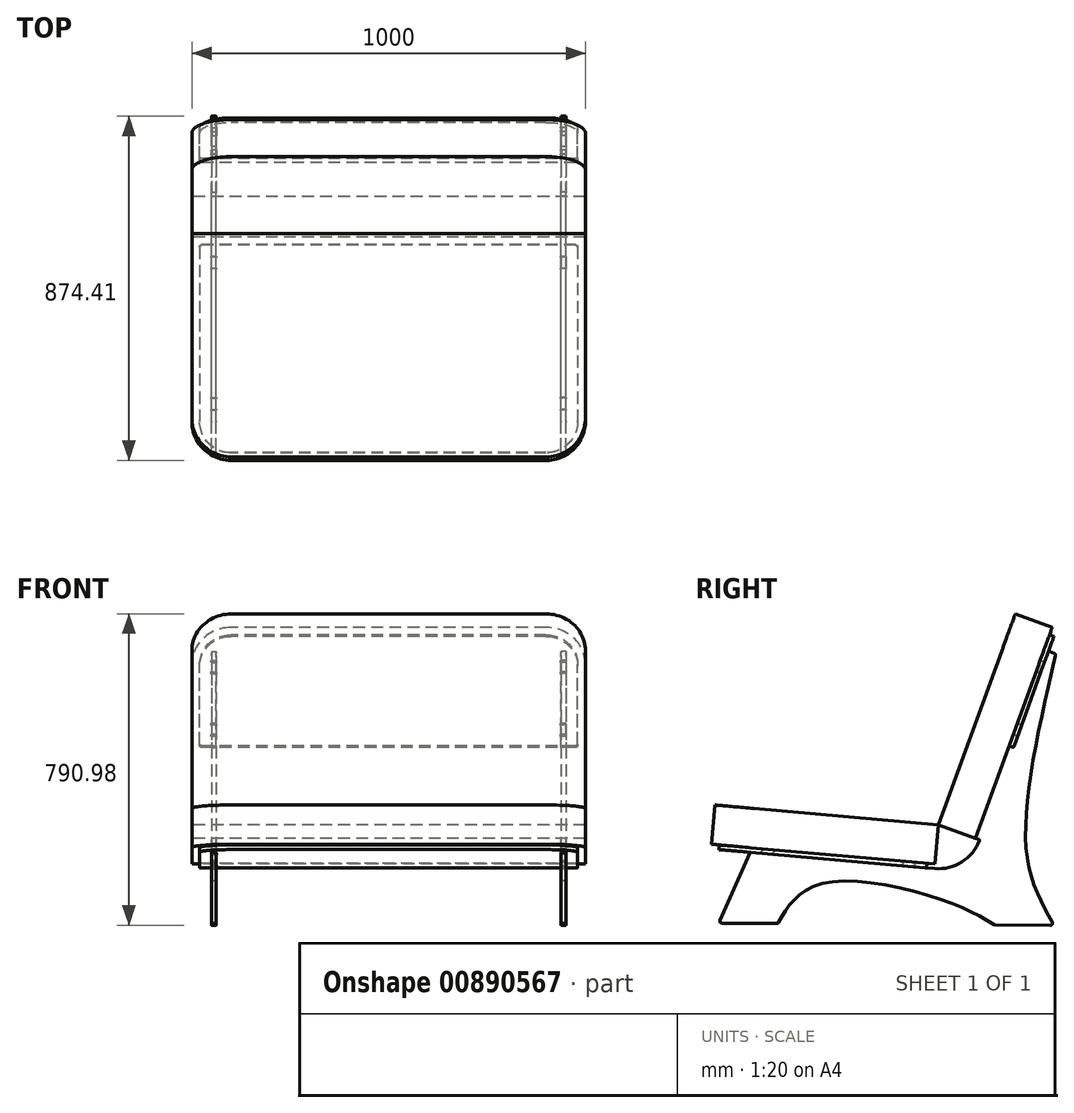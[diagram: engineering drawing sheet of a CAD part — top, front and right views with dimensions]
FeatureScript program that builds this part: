
annotation { "Feature Type Name" : "Feature", "Feature Type Description" : "" }
export const myFeature = defineFeature(function(context is Context, id is Id, definition is map)
    precondition{}
    {
        {
            var Q0;
            Q0=qCreatedBy(makeId("Right.planeOp"),FACE);
            var sketch = newSketch(context, id + "F0", { "sketchPlane" : qUnion([Q0])});
            skLineSegment(sketch, "E0", {"start": v(-759.48, 0) * mm, "end": v(436.3, 0) * mm, "construction": true});
            skLineSegment(sketch, "E1", {"start": v(0, 0) * mm, "end": v(-567.8, 50) * mm});
            skLineSegment(sketch, "E2", {"start": v(-567.8, 50) * mm, "end": v(-567.8, 0) * mm, "construction": true});
            skLineSegment(sketch, "E3.0", {"start": v(8.77, 99.61) * mm, "end": v(-559.03, 149.61) * mm});
            skLineSegment(sketch, "E4", {"start": v(-559.03, 149.61) * mm, "end": v(-567.8, 50) * mm});
            skLineSegment(sketch, "E5", {"start": v(8.77, 99.61) * mm, "end": v(0, 0) * mm});
            skLineSegment(sketch, "E6", {"start": v(8.77, 99.61) * mm, "end": v(204.03, 635.13) * mm});
            skLineSegment(sketch, "E7.0", {"start": v(102.72, 65.36) * mm, "end": v(297.98, 600.87) * mm});
            skLineSegment(sketch, "E8", {"start": v(204.03, 635.13) * mm, "end": v(297.98, 600.87) * mm});
            skLineSegment(sketch, "E9", {"start": v(8.77, 99.61) * mm, "end": v(102.72, 65.36) * mm});
            skSolve(sketch);
        }
        {
            var Q0;
            Q0=makeQuery(id+"F0.imprint","IMPRINT",FACE,{"disambiguationData":[TD([[makeQuery(id+"F0.imprint","IMPRINT",EDGE,{"derivedFrom":sQuery(id+"F0.wireOp",EDGE,"E1")}),-1.0]])]});
            var Q1;
            Q1=makeQuery(id+"F0.imprint","IMPRINT",FACE,{"disambiguationData":[TD([[makeQuery(id+"F0.imprint","IMPRINT",EDGE,{"derivedFrom":sQuery(id+"F0.wireOp",EDGE,"E6")}),-1.0]])]});
            extrude(context, id + "F1", {"entities" : qUnion([Q0, Q1]), "depth" : 500 * mm, "offsetDistance" : 25 * mm, "hasSecondDirection" : true, "secondDirectionOppositeDirection" : true, "secondDirectionDepth" : 500 * mm});
        }
        {
            var Q0;
            Q0=makeQuery(id+"F1.opExtrude","CAP_EDGE",EDGE,{"disambiguationData":[OSD([sQuery(id+"F0.wireOp",EDGE,"E4")])],"isStart":true});
            var Q1;
            Q1=makeQuery(id+"F1.opExtrude","CAP_EDGE",EDGE,{"disambiguationData":[OSD([sQuery(id+"F0.wireOp",EDGE,"E4")])],"isStart":false});
            var Q2;
            Q2=makeQuery(id+"F1.opExtrude","CAP_EDGE",EDGE,{"disambiguationData":[OSD([sQuery(id+"F0.wireOp",EDGE,"E8")])],"isStart":false});
            var Q3;
            Q3=makeQuery(id+"F1.opExtrude","CAP_EDGE",EDGE,{"disambiguationData":[OSD([sQuery(id+"F0.wireOp",EDGE,"E8")])],"isStart":true});
            fillet(context, id + "F2", {"entities" : qUnion([Q0, Q1, Q2, Q3]), "radius" : 100 * mm, "tangentPropagation" : true, "allowEdgeOverflow" : false});
        }
        {
            var Q0;
            Q0=makeQuery(id+"F1.opExtrude","SWEPT_FACE",FACE,{"disambiguationData":[OSD([sQuery(id+"F0.wireOp",EDGE,"E1")])]});
            var sketch = newSketch(context, id + "F3", { "sketchPlane" : qUnion([Q0])});
            skLineSegment(sketch, "E10.0", {"start": v(480, 20) * mm, "end": v(480, 470) * mm});
            skLineSegment(sketch, "E10.1", {"start": v(-480, 20) * mm, "end": v(-480, 470) * mm});
            skArc(sketch, "E10.2", {"start": v(-400, 550) * mm, "mid": v(-456.57, 526.57) * mm, "end": v(-480, 470) * mm});
            skLineSegment(sketch, "E10.3", {"start": v(480, 20) * mm, "end": v(-480, 20) * mm});
            skLineSegment(sketch, "E10.4", {"start": v(400, 550) * mm, "end": v(-400, 550) * mm});
            skArc(sketch, "E10.5", {"start": v(480, 470) * mm, "mid": v(456.57, 526.57) * mm, "end": v(400, 550) * mm});
            skSolve(sketch);
        }
        {
            var Q0;
            Q0=makeQuery(id+"F3.imprint","IMPRINT",FACE,{"disambiguationData":[TD([[makeQuery(id+"F3.imprint","IMPRINT",EDGE,{"derivedFrom":sQuery(id+"F3.wireOp",EDGE,"E10.0")}),1.0]])]});
            extrude(context, id + "F4", {"entities" : qUnion([Q0]), "depth" : 12 * mm, "offsetDistance" : 25 * mm});
        }
        {
            var Q0;
            Q0=makeQuery(id+"F1.opExtrude","SWEPT_FACE",FACE,{"disambiguationData":[OSD([sQuery(id+"F0.wireOp",EDGE,"E7.0")])]});
            var sketch = newSketch(context, id + "F5", { "sketchPlane" : qUnion([Q0])});
            skArc(sketch, "E11.1", {"start": v(-400, 646.6) * mm, "mid": v(-456.57, 623.16) * mm, "end": v(-480, 566.6) * mm});
            skLineSegment(sketch, "E11.2", {"start": v(-400, 646.6) * mm, "end": v(400, 646.6) * mm});
            skLineSegment(sketch, "E11.3", {"start": v(-480, 346.6) * mm, "end": v(-480, 566.6) * mm});
            skArc(sketch, "E11.4", {"start": v(480, 566.6) * mm, "mid": v(456.57, 623.16) * mm, "end": v(400, 646.6) * mm});
            skLineSegment(sketch, "E11.5", {"start": v(480, 346.6) * mm, "end": v(480, 566.6) * mm});
            skLineSegment(sketch, "E12.0", {"start": v(-480, 346.6) * mm, "end": v(480, 346.6) * mm});
            skSolve(sketch);
        }
        {
            var Q0;
            Q0=makeQuery(id+"F5.imprint","IMPRINT",FACE,{"disambiguationData":[TD([[makeQuery(id+"F5.imprint","IMPRINT",EDGE,{"derivedFrom":sQuery(id+"F5.wireOp",EDGE,"E11.1")}),1.0]])]});
            extrude(context, id + "F6", {"entities" : qUnion([Q0]), "depth" : 12 * mm, "offsetDistance" : 25 * mm});
        }
        {
            var Q0;
            Q0=qCreatedBy(makeId("Right.planeOp"),FACE);
            var sketch = newSketch(context, id + "F7", { "sketchPlane" : qUnion([Q0])});
            skLineSegment(sketch, "E13.0.0", {"start": v(-19.92, 1.75) * mm, "end": v(-468.19, 41.23) * mm, "construction": true});
            skLineSegment(sketch, "E13.0.1", {"start": v(-468.19, 41.23) * mm, "end": v(-469.24, 29.27) * mm, "construction": true});
            skLineSegment(sketch, "E13.0.2", {"start": v(-469.24, 29.27) * mm, "end": v(-20.98, -10.2) * mm, "construction": true});
            skLineSegment(sketch, "E13.0.3", {"start": v(-20.98, -10.2) * mm, "end": v(-19.92, 1.75) * mm, "construction": true});
            skLineSegment(sketch, "E14.0.0", {"start": v(204.03, 635.13) * mm, "end": v(169.77, 541.18) * mm, "construction": true});
            skLineSegment(sketch, "E14.0.3", {"start": v(297.98, 600.87) * mm, "end": v(204.03, 635.13) * mm, "construction": true});
            skLineSegment(sketch, "E14.1.2", {"start": v(169.77, 541.18) * mm, "end": v(8.77, 99.61) * mm, "construction": true});
            skLineSegment(sketch, "E14.1.3", {"start": v(8.77, 99.61) * mm, "end": v(102.72, 65.36) * mm, "construction": true});
            skLineSegment(sketch, "E14.2.0", {"start": v(8.77, 99.61) * mm, "end": v(-459.42, 140.84) * mm, "construction": true});
            skLineSegment(sketch, "E14.2.1", {"start": v(-459.42, 140.84) * mm, "end": v(-468.19, 41.23) * mm, "construction": true});
            skLineSegment(sketch, "E14.2.2", {"start": v(-468.19, 41.23) * mm, "end": v(0, 0) * mm, "construction": true});
            skLineSegment(sketch, "E14.2.3", {"start": v(0, 0) * mm, "end": v(8.77, 99.61) * mm, "construction": true});
            skLineSegment(sketch, "E14.3.0", {"start": v(-559.03, 149.61) * mm, "end": v(-459.42, 140.84) * mm, "construction": true});
            skLineSegment(sketch, "E14.3.1", {"start": v(-567.8, 50) * mm, "end": v(-559.03, 149.61) * mm, "construction": true});
            skLineSegment(sketch, "E14.3.2", {"start": v(-567.8, 50) * mm, "end": v(-468.19, 41.23) * mm, "construction": true});
            skLineSegment(sketch, "E14.3.3", {"start": v(-468.19, 41.23) * mm, "end": v(-459.42, 140.84) * mm, "construction": true});
            skLineSegment(sketch, "E15.0", {"start": v(-759.48, 0) * mm, "end": v(436.3, 0) * mm, "construction": true});
            skLineSegment(sketch, "E16", {"start": v(-559.03, 149.61) * mm, "end": v(812.25, 140.84) * mm, "construction": true});
            skLineSegment(sketch, "E17.0", {"start": v(-560.95, -150.38) * mm, "end": v(810.34, -159.15) * mm, "construction": true});
            skLineSegment(sketch, "E18.0.0", {"start": v(-468.19, 41.23) * mm, "end": v(-547.88, 48.25) * mm, "construction": true});
            skLineSegment(sketch, "E18.0.1", {"start": v(-547.88, 48.25) * mm, "end": v(-548.93, 36.3) * mm, "construction": true});
            skLineSegment(sketch, "E18.0.2", {"start": v(-548.93, 36.3) * mm, "end": v(-469.24, 29.27) * mm, "construction": true});
            skLineSegment(sketch, "E19.0.0", {"start": v(291.13, 582.08) * mm, "end": v(263.72, 506.92) * mm, "construction": true});
            skLineSegment(sketch, "E19.0.3", {"start": v(302.4, 577.97) * mm, "end": v(291.13, 582.08) * mm, "construction": true});
            skLineSegment(sketch, "E20", {"start": v(-548.93, 36.3) * mm, "end": v(-548.93, -280.6) * mm, "construction": true});
            skLineSegment(sketch, "E21", {"start": v(-548.93, -150.46) * mm, "end": v(-469.24, 29.27) * mm});
            skLineSegment(sketch, "E22", {"start": v(302.4, 577.97) * mm, "end": v(302.4, -479.36) * mm, "construction": true});
            skLineSegment(sketch, "E23", {"start": v(-469.24, 29.27) * mm, "end": v(-439.36, 26.64) * mm});
            skLineSegment(sketch, "E24", {"start": v(-439.36, 26.64) * mm, "end": v(-438.3, 38.6) * mm});
            skLineSegment(sketch, "E25", {"start": v(-438.3, 38.6) * mm, "end": v(-408.42, 35.96) * mm});
            skLineSegment(sketch, "E26", {"start": v(-408.42, 35.96) * mm, "end": v(-409.47, 24.01) * mm});
            skLineSegment(sketch, "E27", {"start": v(-20.98, -10.2) * mm, "end": v(-50.86, -7.57) * mm});
            skLineSegment(sketch, "E28", {"start": v(-50.86, -7.57) * mm, "end": v(-49.8, 4.39) * mm});
            skLineSegment(sketch, "E29", {"start": v(-49.8, 4.39) * mm, "end": v(-79.7, 7.02) * mm});
            skLineSegment(sketch, "E30", {"start": v(-79.7, 7.02) * mm, "end": v(-80.74, -4.94) * mm});
            skLineSegment(sketch, "E31", {"start": v(-80.74, -4.94) * mm, "end": v(-409.47, 24.01) * mm});
            skLineSegment(sketch, "E32", {"start": v(-548.93, -150.46) * mm, "end": v(-398.94, -151.42) * mm});
            skLineSegment(sketch, "E33", {"start": v(302.4, -155.9) * mm, "end": v(152.4, -154.94) * mm});
            skFitSpline(sketch, "E34", {"points": [v(-398.94, -151.42) * mm, v(-357.7, -91.47) * mm, v(-259.83, -45.2) * mm, v(19.54, -91.47) * mm, v(152.4, -154.94) * mm], "startDerivative": vector(200.43, 350.59) * mm, "endDerivative": vector(440.32, -254.58) * mm});
            skLineSegment(sketch, "E35", {"start": v(302.4, 577.97) * mm, "end": v(288.7, 540.4) * mm, "construction": true});
            skLineSegment(sketch, "E36", {"start": v(199.63, 296.12) * mm, "end": v(209.91, 324.3) * mm});
            skLineSegment(sketch, "E37", {"start": v(209.91, 324.3) * mm, "end": v(198.64, 328.42) * mm});
            skLineSegment(sketch, "E38", {"start": v(198.64, 328.42) * mm, "end": v(208.91, 356.6) * mm});
            skLineSegment(sketch, "E39", {"start": v(208.91, 356.6) * mm, "end": v(220.19, 352.5) * mm});
            skLineSegment(sketch, "E40", {"start": v(288.7, 540.4) * mm, "end": v(307.49, 533.54) * mm});
            skFitSpline(sketch, "E41", {"points": [v(307.49, 533.54) * mm, v(232.67, 31.44) * mm, v(302.4, -155.9) * mm], "startDerivative": vector(-214.75, -918.96) * mm, "endDerivative": vector(239.2, -422.01) * mm});
            skLineSegment(sketch, "E42", {"start": v(288.7, 540.4) * mm, "end": v(278.42, 512.2) * mm});
            skLineSegment(sketch, "E43", {"start": v(278.42, 512.2) * mm, "end": v(267.15, 516.32) * mm});
            skLineSegment(sketch, "E44", {"start": v(267.15, 516.32) * mm, "end": v(256.87, 488.13) * mm});
            skLineSegment(sketch, "E45", {"start": v(256.87, 488.13) * mm, "end": v(268.14, 484.02) * mm});
            skLineSegment(sketch, "E46", {"start": v(268.14, 484.02) * mm, "end": v(220.19, 352.5) * mm});
            skLineSegment(sketch, "E47", {"start": v(-20.98, -10.2) * mm, "end": v(-1.05, -11.95) * mm});
            skLineSegment(sketch, "E48", {"start": v(102.72, 65.36) * mm, "end": v(256.87, 488.13) * mm, "construction": true});
            skLineSegment(sketch, "E49", {"start": v(199.63, 296.12) * mm, "end": v(188.36, 300.23) * mm});
            skLineSegment(sketch, "E50", {"start": v(188.36, 300.23) * mm, "end": v(102.72, 65.36) * mm});
            skLineSegment(sketch, "E51", {"start": v(102.72, 65.36) * mm, "end": v(114, 61.25) * mm});
            skArc(sketch, "E52.trimOffspring", {"start": v(-1.05, -11.95) * mm, "mid": v(68.9, 5.12) * mm, "end": v(114, 61.25) * mm});
            skSolve(sketch);
        }
        {
            var Q0;
            Q0=makeQuery(id+"F7.imprint","IMPRINT",FACE,{"disambiguationData":[TD([[makeQuery(id+"F7.imprint","IMPRINT",EDGE,{"derivedFrom":sQuery(id+"F7.wireOp",EDGE,"E21")}),-1.0]])]});
            extrude(context, id + "F8", {"entities" : qUnion([Q0]), "depth" : 450 * mm, "offsetDistance" : 25 * mm, "hasSecondDirection" : true, "secondDirectionOppositeDirection" : false, "secondDirectionDepth" : 438 * mm});
        }
        {
            var Q0;
            Q0=makeQuery(id+"F8.opExtrude","SWEPT_FACE",FACE,{"disambiguationData":[OSD([sQuery(id+"F7.wireOp",EDGE,"E29")])]});
            var sketch = newSketch(context, id + "F9", { "sketchPlane" : qUnion([Q0])});
            skArc(sketch, "E53", {"start": v(438, -79) * mm, "mid": v(437.3, -80.7) * mm, "end": v(439, -80) * mm});
            skArc(sketch, "E54", {"start": v(439, -50) * mm, "mid": v(437.3, -49.3) * mm, "end": v(438, -51) * mm});
            skArc(sketch, "E55", {"start": v(450, -51) * mm, "mid": v(450.7, -49.3) * mm, "end": v(449, -50) * mm});
            skArc(sketch, "E56", {"start": v(449, -80) * mm, "mid": v(450.7, -80.7) * mm, "end": v(450, -79) * mm});
            skLineSegment(sketch, "E57.bottom", {"start": v(439, -80) * mm, "end": v(449, -80) * mm});
            skLineSegment(sketch, "E57.top", {"start": v(439, -50) * mm, "end": v(449, -50) * mm});
            skLineSegment(sketch, "E57.left", {"start": v(438, -79) * mm, "end": v(438, -51) * mm});
            skLineSegment(sketch, "E57.right", {"start": v(450, -79) * mm, "end": v(450, -51) * mm});
            skLineSegment(sketch, "E58.0", {"start": v(438, -439) * mm, "end": v(438, -411) * mm});
            skLineSegment(sketch, "E58.1", {"start": v(449, -440) * mm, "end": v(439, -440) * mm});
            skLineSegment(sketch, "E58.2", {"start": v(449, -410) * mm, "end": v(439, -410) * mm});
            skLineSegment(sketch, "E58.3", {"start": v(450, -439) * mm, "end": v(450, -411) * mm});
            skArc(sketch, "E59", {"start": v(438, -439) * mm, "mid": v(437.3, -440.7) * mm, "end": v(439, -440) * mm});
            skArc(sketch, "E60", {"start": v(439, -410) * mm, "mid": v(437.3, -409.3) * mm, "end": v(438, -411) * mm});
            skArc(sketch, "E61", {"start": v(450, -411) * mm, "mid": v(450.7, -409.3) * mm, "end": v(449, -410) * mm});
            skArc(sketch, "E62", {"start": v(449, -440) * mm, "mid": v(450.7, -440.7) * mm, "end": v(450, -439) * mm});
            skArc(sketch, "E63.MirrorCS", {"start": v(-450, -411) * mm, "mid": v(-450.7, -409.3) * mm, "end": v(-449, -410) * mm});
            skLineSegment(sketch, "E64.MirrorCS", {"start": v(-449, -410) * mm, "end": v(-439, -410) * mm});
            skArc(sketch, "E65.MirrorCS", {"start": v(-439, -410) * mm, "mid": v(-437.3, -409.3) * mm, "end": v(-438, -411) * mm});
            skLineSegment(sketch, "E66.MirrorCS", {"start": v(-450, -439) * mm, "end": v(-450, -411) * mm});
            skArc(sketch, "E67.MirrorCS", {"start": v(-449, -440) * mm, "mid": v(-450.7, -440.7) * mm, "end": v(-450, -439) * mm});
            skLineSegment(sketch, "E68.MirrorCS", {"start": v(-438, -439) * mm, "end": v(-438, -411) * mm});
            skArc(sketch, "E69.MirrorCS", {"start": v(-438, -439) * mm, "mid": v(-437.3, -440.7) * mm, "end": v(-439, -440) * mm});
            skLineSegment(sketch, "E70.MirrorCS", {"start": v(-449, -440) * mm, "end": v(-439, -440) * mm});
            skArc(sketch, "E71.MirrorCS", {"start": v(-449, -80) * mm, "mid": v(-450.7, -80.7) * mm, "end": v(-450, -79) * mm});
            skLineSegment(sketch, "E72.MirrorCS", {"start": v(-439, -80) * mm, "end": v(-449, -80) * mm});
            skArc(sketch, "E73.MirrorCS", {"start": v(-438, -79) * mm, "mid": v(-437.3, -80.7) * mm, "end": v(-439, -80) * mm});
            skArc(sketch, "E74.MirrorCS", {"start": v(-439, -50) * mm, "mid": v(-437.3, -49.3) * mm, "end": v(-438, -51) * mm});
            skLineSegment(sketch, "E75.MirrorCS", {"start": v(-438, -79) * mm, "end": v(-438, -51) * mm});
            skLineSegment(sketch, "E76.MirrorCS", {"start": v(-439, -50) * mm, "end": v(-449, -50) * mm});
            skLineSegment(sketch, "E77.MirrorCS", {"start": v(-450, -79) * mm, "end": v(-450, -51) * mm});
            skArc(sketch, "E78.MirrorCS", {"start": v(-450, -51) * mm, "mid": v(-450.7, -49.3) * mm, "end": v(-449, -50) * mm});
            skSolve(sketch);
        }
        {
            var Q0;
            Q0 = qSketchRegion(id + "F9", true);
            extrude(context, id + "F10", {"entities" : qUnion([Q0]), "operationType" : NewBodyOperationType.REMOVE, "endBound" : BoundingType.UP_TO_NEXT, "oppositeDirection" : true, "depth" : 25 * mm, "offsetDistance" : 25 * mm});
        }
        {
            var Q0;
            Q0=makeQuery(id+"F8.opExtrude","SWEPT_FACE",FACE,{"disambiguationData":[OSD([sQuery(id+"F7.wireOp",EDGE,"E38")])]});
            var sketch = newSketch(context, id + "F11", { "sketchPlane" : qUnion([Q0])});
            skLineSegment(sketch, "E79.bottom", {"start": v(439, 406.6) * mm, "end": v(449, 406.6) * mm});
            skLineSegment(sketch, "E79.top", {"start": v(439, 376.6) * mm, "end": v(449, 376.6) * mm});
            skLineSegment(sketch, "E79.left", {"start": v(438, 405.6) * mm, "end": v(438, 377.6) * mm});
            skLineSegment(sketch, "E79.right", {"start": v(450, 405.6) * mm, "end": v(450, 377.6) * mm});
            skArc(sketch, "E80", {"start": v(450, 405.6) * mm, "mid": v(450.7, 407.3) * mm, "end": v(449, 406.6) * mm});
            skArc(sketch, "E81", {"start": v(439, 406.6) * mm, "mid": v(437.3, 407.3) * mm, "end": v(438, 405.6) * mm});
            skArc(sketch, "E82", {"start": v(438, 377.6) * mm, "mid": v(437.3, 375.89) * mm, "end": v(439, 376.6) * mm});
            skArc(sketch, "E83", {"start": v(449, 376.6) * mm, "mid": v(450.7, 375.89) * mm, "end": v(450, 377.6) * mm});
            skLineSegment(sketch, "E84.0", {"start": v(449, 576.6) * mm, "end": v(439, 576.6) * mm});
            skLineSegment(sketch, "E84.1", {"start": v(438, 575.6) * mm, "end": v(438, 547.6) * mm});
            skLineSegment(sketch, "E84.2", {"start": v(450, 575.6) * mm, "end": v(450, 547.6) * mm});
            skLineSegment(sketch, "E84.3", {"start": v(449, 546.6) * mm, "end": v(439, 546.6) * mm});
            skArc(sketch, "E85", {"start": v(439, 576.6) * mm, "mid": v(437.3, 577.3) * mm, "end": v(438, 575.6) * mm});
            skArc(sketch, "E86", {"start": v(450, 575.6) * mm, "mid": v(450.7, 577.3) * mm, "end": v(449, 576.6) * mm});
            skArc(sketch, "E87", {"start": v(449, 546.6) * mm, "mid": v(450.7, 545.89) * mm, "end": v(450, 547.6) * mm});
            skArc(sketch, "E88", {"start": v(438, 547.6) * mm, "mid": v(437.3, 545.89) * mm, "end": v(439, 546.6) * mm});
            skArc(sketch, "E89.MirrorCS", {"start": v(-438, 547.6) * mm, "mid": v(-437.3, 545.89) * mm, "end": v(-439, 546.6) * mm});
            skLineSegment(sketch, "E90.MirrorCS", {"start": v(-449, 576.6) * mm, "end": v(-439, 576.6) * mm});
            skLineSegment(sketch, "E91.MirrorCS", {"start": v(-449, 546.6) * mm, "end": v(-439, 546.6) * mm});
            skArc(sketch, "E92.MirrorCS", {"start": v(-450, 575.6) * mm, "mid": v(-450.7, 577.3) * mm, "end": v(-449, 576.6) * mm});
            skArc(sketch, "E93.MirrorCS", {"start": v(-449, 546.6) * mm, "mid": v(-450.7, 545.89) * mm, "end": v(-450, 547.6) * mm});
            skArc(sketch, "E94.MirrorCS", {"start": v(-439, 576.6) * mm, "mid": v(-437.3, 577.3) * mm, "end": v(-438, 575.6) * mm});
            skLineSegment(sketch, "E95.MirrorCS", {"start": v(-438, 575.6) * mm, "end": v(-438, 547.6) * mm});
            skLineSegment(sketch, "E96.MirrorCS", {"start": v(-450, 575.6) * mm, "end": v(-450, 547.6) * mm});
            skArc(sketch, "E97.MirrorCS", {"start": v(-438, 377.6) * mm, "mid": v(-437.3, 375.89) * mm, "end": v(-439, 376.6) * mm});
            skArc(sketch, "E98.MirrorCS", {"start": v(-449, 376.6) * mm, "mid": v(-450.7, 375.89) * mm, "end": v(-450, 377.6) * mm});
            skArc(sketch, "E99.MirrorCS", {"start": v(-439, 406.6) * mm, "mid": v(-437.3, 407.3) * mm, "end": v(-438, 405.6) * mm});
            skArc(sketch, "E100.MirrorCS", {"start": v(-450, 405.6) * mm, "mid": v(-450.7, 407.3) * mm, "end": v(-449, 406.6) * mm});
            skLineSegment(sketch, "E101.MirrorCS", {"start": v(-439, 376.6) * mm, "end": v(-449, 376.6) * mm});
            skLineSegment(sketch, "E102.MirrorCS", {"start": v(-439, 406.6) * mm, "end": v(-449, 406.6) * mm});
            skLineSegment(sketch, "E103.MirrorCS", {"start": v(-450, 405.6) * mm, "end": v(-450, 377.6) * mm});
            skLineSegment(sketch, "E104.MirrorCS", {"start": v(-438, 405.6) * mm, "end": v(-438, 377.6) * mm});
            skSolve(sketch);
        }
        {
            var Q0;
            Q0 = qSketchRegion(id + "F11", true);
            extrude(context, id + "F12", {"entities" : qUnion([Q0]), "operationType" : NewBodyOperationType.REMOVE, "endBound" : BoundingType.UP_TO_NEXT, "oppositeDirection" : true, "depth" : 25 * mm, "offsetDistance" : 25 * mm});
        }
        {
            var Q0;
            Q0=makeQuery(id+"F8.opExtrude","SWEPT_EDGE",EDGE,{"disambiguationData":[OSD([sQuery(id+"F7.wireOp",EDGE,"E21"),sQuery(id+"F7.wireOp",EDGE,"E32")])]});
            var Q1;
            Q1=makeQuery(id+"F8.opExtrude","SWEPT_EDGE",EDGE,{"disambiguationData":[OSD([sQuery(id+"F7.wireOp",EDGE,"E32"),sQuery(id+"F7.wireOp",EDGE,"E34")])]});
            var Q2;
            Q2=makeQuery(id+"F8.opExtrude","SWEPT_EDGE",EDGE,{"disambiguationData":[OSD([sQuery(id+"F7.wireOp",EDGE,"E33"),sQuery(id+"F7.wireOp",EDGE,"E34")])]});
            var Q3;
            Q3=makeQuery(id+"F8.opExtrude","SWEPT_EDGE",EDGE,{"disambiguationData":[OSD([sQuery(id+"F7.wireOp",EDGE,"E33"),sQuery(id+"F7.wireOp",EDGE,"E41")])]});
            var Q4;
            Q4=makeQuery(id+"F8.opExtrude","SWEPT_EDGE",EDGE,{"disambiguationData":[OSD([sQuery(id+"F7.wireOp",EDGE,"E40"),sQuery(id+"F7.wireOp",EDGE,"E41")])]});
            fillet(context, id + "F13", {"entities" : qUnion([Q0, Q1, Q2, Q3, Q4]), "radius" : 5 * mm, "tangentPropagation" : true, "allowEdgeOverflow" : false});
        }
        {
            var Q0;
            Q0=makeQuery(id+"F8.opExtrude","SWEPT_EDGE",EDGE,{"disambiguationData":[OSD([sQuery(id+"F7.wireOp",EDGE,"E21"),sQuery(id+"F7.wireOp",EDGE,"E23")])]});
            var Q1;
            Q1=makeQuery(id+"F8.opExtrude","SWEPT_EDGE",EDGE,{"disambiguationData":[OSD([sQuery(id+"F7.wireOp",EDGE,"E24"),sQuery(id+"F7.wireOp",EDGE,"E25")])]});
            var Q2;
            Q2=makeQuery(id+"F8.opExtrude","SWEPT_EDGE",EDGE,{"disambiguationData":[OSD([sQuery(id+"F7.wireOp",EDGE,"E25"),sQuery(id+"F7.wireOp",EDGE,"E26")])]});
            var Q3;
            Q3=makeQuery(id+"F8.opExtrude","SWEPT_EDGE",EDGE,{"disambiguationData":[OSD([sQuery(id+"F7.wireOp",EDGE,"E29"),sQuery(id+"F7.wireOp",EDGE,"E30")])]});
            var Q4;
            Q4=makeQuery(id+"F8.opExtrude","SWEPT_EDGE",EDGE,{"disambiguationData":[OSD([sQuery(id+"F7.wireOp",EDGE,"E28"),sQuery(id+"F7.wireOp",EDGE,"E29")])]});
            var Q5;
            Q5=makeQuery(id+"F8.opExtrude","SWEPT_EDGE",EDGE,{"disambiguationData":[OSD([sQuery(id+"F7.wireOp",EDGE,"E51"),sQuery(id+"F7.wireOp",EDGE,"E52.trimOffspring")])]});
            var Q6;
            Q6=makeQuery(id+"F8.opExtrude","SWEPT_EDGE",EDGE,{"disambiguationData":[OSD([sQuery(id+"F7.wireOp",EDGE,"E50"),sQuery(id+"F7.wireOp",EDGE,"E51")])]});
            var Q7;
            Q7=makeQuery(id+"F8.opExtrude","SWEPT_EDGE",EDGE,{"disambiguationData":[OSD([sQuery(id+"F7.wireOp",EDGE,"E49"),sQuery(id+"F7.wireOp",EDGE,"E50")])]});
            var Q8;
            Q8=makeQuery(id+"F8.opExtrude","SWEPT_EDGE",EDGE,{"disambiguationData":[OSD([sQuery(id+"F7.wireOp",EDGE,"E37"),sQuery(id+"F7.wireOp",EDGE,"E38")])]});
            var Q9;
            Q9=makeQuery(id+"F8.opExtrude","SWEPT_EDGE",EDGE,{"disambiguationData":[OSD([sQuery(id+"F7.wireOp",EDGE,"E38"),sQuery(id+"F7.wireOp",EDGE,"E39")])]});
            var Q10;
            Q10=makeQuery(id+"F8.opExtrude","SWEPT_EDGE",EDGE,{"disambiguationData":[OSD([sQuery(id+"F7.wireOp",EDGE,"E44"),sQuery(id+"F7.wireOp",EDGE,"E45")])]});
            var Q11;
            Q11=makeQuery(id+"F8.opExtrude","SWEPT_EDGE",EDGE,{"disambiguationData":[OSD([sQuery(id+"F7.wireOp",EDGE,"E43"),sQuery(id+"F7.wireOp",EDGE,"E44")])]});
            var Q12;
            Q12=makeQuery(id+"F8.opExtrude","SWEPT_EDGE",EDGE,{"disambiguationData":[OSD([sQuery(id+"F7.wireOp",EDGE,"E40"),sQuery(id+"F7.wireOp",EDGE,"E42")])]});
            fillet(context, id + "F14", {"entities" : qUnion([Q0, Q1, Q2, Q3, Q4, Q5, Q6, Q7, Q8, Q9, Q10, Q11, Q12]), "radius" : 2 * mm, "tangentPropagation" : true, "allowEdgeOverflow" : false});
        }
        {
            var Q0;
            Q0=makeQuery(id+"F6.opExtrude","SWEPT_EDGE",EDGE,{"disambiguationData":[OSD([sQuery(id+"F5.wireOp",EDGE,"E11.3"),sQuery(id+"F5.wireOp",EDGE,"E12.0")])]});
            var Q1;
            Q1=makeQuery(id+"F6.opExtrude","SWEPT_EDGE",EDGE,{"disambiguationData":[OSD([sQuery(id+"F5.wireOp",EDGE,"E11.5"),sQuery(id+"F5.wireOp",EDGE,"E12.0")])]});
            var Q2;
            Q2=makeQuery(id+"F4.opExtrude","SWEPT_EDGE",EDGE,{"disambiguationData":[OSD([sQuery(id+"F3.wireOp",EDGE,"E10.1"),sQuery(id+"F3.wireOp",EDGE,"E10.3")])]});
            var Q3;
            Q3=makeQuery(id+"F4.opExtrude","SWEPT_EDGE",EDGE,{"disambiguationData":[OSD([sQuery(id+"F3.wireOp",EDGE,"E10.0"),sQuery(id+"F3.wireOp",EDGE,"E10.3")])]});
            fillet(context, id + "F15", {"entities" : qUnion([Q0, Q1, Q2, Q3]), "radius" : 5 * mm, "tangentPropagation" : true, "allowEdgeOverflow" : false});
        }
        {
            var Q0;
            Q0=makeQuery(id+"F8.opExtrude","SWEPT_BODY",BODY,{"disambiguationData":[OSD([sQuery(id+"F7.wireOp",EDGE,"E21"),sQuery(id+"F7.wireOp",EDGE,"E23"),sQuery(id+"F7.wireOp",EDGE,"E24"),sQuery(id+"F7.wireOp",EDGE,"E25"),sQuery(id+"F7.wireOp",EDGE,"E26"),sQuery(id+"F7.wireOp",EDGE,"E27"),sQuery(id+"F7.wireOp",EDGE,"E28"),sQuery(id+"F7.wireOp",EDGE,"E29"),sQuery(id+"F7.wireOp",EDGE,"E30"),sQuery(id+"F7.wireOp",EDGE,"E31"),sQuery(id+"F7.wireOp",EDGE,"E32"),sQuery(id+"F7.wireOp",EDGE,"E33"),sQuery(id+"F7.wireOp",EDGE,"E34"),sQuery(id+"F7.wireOp",EDGE,"E36"),sQuery(id+"F7.wireOp",EDGE,"E37"),sQuery(id+"F7.wireOp",EDGE,"E38"),sQuery(id+"F7.wireOp",EDGE,"E39"),sQuery(id+"F7.wireOp",EDGE,"E40"),sQuery(id+"F7.wireOp",EDGE,"E41"),sQuery(id+"F7.wireOp",EDGE,"E42"),sQuery(id+"F7.wireOp",EDGE,"E43"),sQuery(id+"F7.wireOp",EDGE,"E44"),sQuery(id+"F7.wireOp",EDGE,"E45"),sQuery(id+"F7.wireOp",EDGE,"E46"),sQuery(id+"F7.wireOp",EDGE,"E47"),sQuery(id+"F7.wireOp",EDGE,"E49"),sQuery(id+"F7.wireOp",EDGE,"E50"),sQuery(id+"F7.wireOp",EDGE,"E51"),sQuery(id+"F7.wireOp",EDGE,"E52.trimOffspring")])]});
            var Q1;
            Q1=qCreatedBy(makeId("Right.planeOp"),FACE);
            mirror(context, id + "F16", {"entities" : qUnion([Q0]), "mirrorPlane" : qUnion([Q1])});
        }
    });
